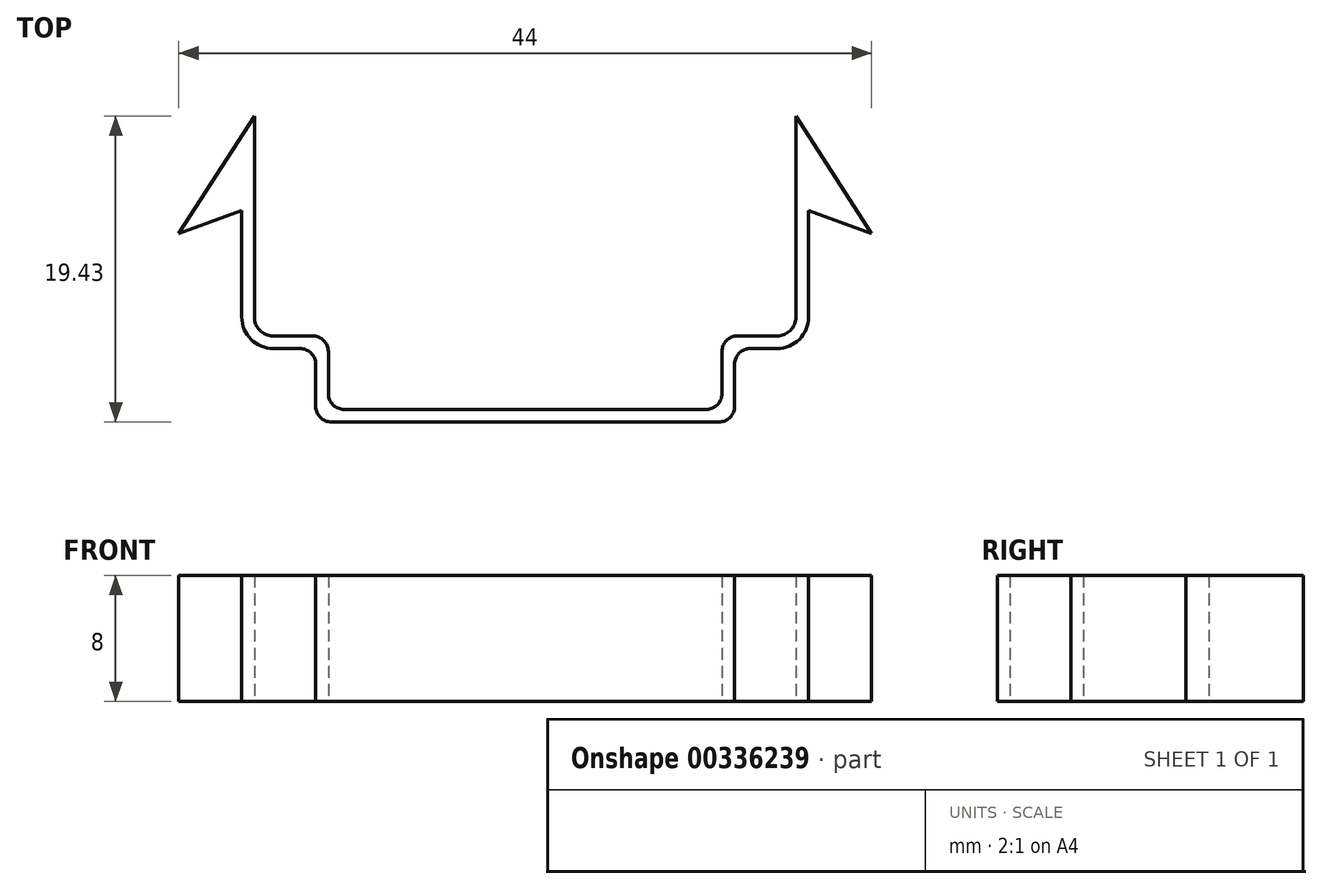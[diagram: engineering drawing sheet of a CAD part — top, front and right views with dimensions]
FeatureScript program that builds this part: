
annotation { "Feature Type Name" : "Feature", "Feature Type Description" : "" }
export const myFeature = defineFeature(function(context is Context, id is Id, definition is map)
    precondition{}
    {
        {
            var Q0;
            Q0=qCreatedBy(makeId("Top.planeOp"),FACE);
            var sketch = newSketch(context, id + "F0", { "sketchPlane" : qUnion([Q0])});
            skLineSegment(sketch, "E0.bottom", {"start": v(-12.5, 0) * mm, "end": v(12.5, 0) * mm});
            skLineSegment(sketch, "E0.top", {"start": v(-12.5, -7.73) * mm, "end": v(12.5, -7.73) * mm});
            skLineSegment(sketch, "E0.left", {"start": v(-12.5, 0) * mm, "end": v(-12.5, -7.73) * mm});
            skLineSegment(sketch, "E0.right", {"start": v(12.5, 0) * mm, "end": v(12.5, -7.73) * mm});
            skLineSegment(sketch, "E1.bottom", {"start": v(-18, 0) * mm, "end": v(-26.07, 0) * mm});
            skLineSegment(sketch, "E1.top", {"start": v(-18, 4.9) * mm, "end": v(-26.07, 4.9) * mm});
            skLineSegment(sketch, "E1.left", {"start": v(-18, 0) * mm, "end": v(-18, 4.9) * mm});
            skLineSegment(sketch, "E1.right", {"start": v(-26.07, 0) * mm, "end": v(-26.07, 4.9) * mm});
            skLineSegment(sketch, "E2.MirrorCS", {"start": v(18, 0) * mm, "end": v(18, 4.9) * mm});
            skLineSegment(sketch, "E3.MirrorCS", {"start": v(18, 4.9) * mm, "end": v(26.07, 4.9) * mm});
            skLineSegment(sketch, "E4.MirrorCS", {"start": v(26.07, 0) * mm, "end": v(26.07, 4.9) * mm});
            skLineSegment(sketch, "E5.MirrorCS", {"start": v(18, 0) * mm, "end": v(26.07, 0) * mm});
            skSolve(sketch);
        }
        {
            var Q0;
            Q0=qCreatedBy(makeId("Top.planeOp"),FACE);
            var sketch = newSketch(context, id + "F1", { "sketchPlane" : qUnion([Q0])});
            skLineSegment(sketch, "E6.0.0", {"start": v(-12.5, 0) * mm, "end": v(-12.5, -7.73) * mm, "construction": true});
            skLineSegment(sketch, "E6.0.1", {"start": v(-12.5, -7.73) * mm, "end": v(12.5, -7.73) * mm, "construction": true});
            skLineSegment(sketch, "E6.0.2", {"start": v(12.5, -7.73) * mm, "end": v(12.5, 0) * mm, "construction": true});
            skLineSegment(sketch, "E6.0.3", {"start": v(12.5, 0) * mm, "end": v(-12.5, 0) * mm, "construction": true});
            skLineSegment(sketch, "E7.0.0", {"start": v(-18, 0) * mm, "end": v(-18, 4.9) * mm, "construction": true});
            skLineSegment(sketch, "E7.0.1", {"start": v(-18, 4.9) * mm, "end": v(-26.07, 4.9) * mm, "construction": true});
            skLineSegment(sketch, "E7.0.2", {"start": v(-26.07, 4.9) * mm, "end": v(-26.07, 0) * mm, "construction": true});
            skLineSegment(sketch, "E7.0.3", {"start": v(-26.07, 0) * mm, "end": v(-18, 0) * mm, "construction": true});
            skLineSegment(sketch, "E8.0.0", {"start": v(18, 4.9) * mm, "end": v(18, 0) * mm, "construction": true});
            skLineSegment(sketch, "E8.0.1", {"start": v(18, 0) * mm, "end": v(26.07, 0) * mm, "construction": true});
            skLineSegment(sketch, "E8.0.2", {"start": v(26.07, 0) * mm, "end": v(26.07, 4.9) * mm, "construction": true});
            skLineSegment(sketch, "E8.0.3", {"start": v(26.07, 4.9) * mm, "end": v(18, 4.9) * mm, "construction": true});
            skLineSegment(sketch, "E9", {"start": v(-12.5, -3.87) * mm, "end": v(-16, -3.87) * mm});
            skLineSegment(sketch, "E10", {"start": v(-18, -1.87) * mm, "end": v(-18, 4.9) * mm});
            skLineSegment(sketch, "E11", {"start": v(-18, 4.9) * mm, "end": v(-22, 3.44) * mm});
            skLineSegment(sketch, "E12", {"start": v(-22, 3.44) * mm, "end": v(-17.2, 10.9) * mm});
            skPoint(sketch, "E13.visualSharp", {"position": v(-18, -3.87) * mm});
            skArc(sketch, "E13.filletArc", {"start": v(-18, -1.87) * mm, "mid": v(-17.41, -3.28) * mm, "end": v(-16, -3.87) * mm});
            skLineSegment(sketch, "E14.0", {"start": v(-17.2, -1.87) * mm, "end": v(-17.2, 10.9) * mm});
            skArc(sketch, "E14.1", {"start": v(-17.2, -1.87) * mm, "mid": v(-16.85, -2.71) * mm, "end": v(-16, -3.07) * mm});
            skLineSegment(sketch, "E14.2", {"start": v(-12.5, -3.07) * mm, "end": v(-16, -3.07) * mm});
            skLineSegment(sketch, "E15", {"start": v(-12.5, -3.07) * mm, "end": v(-12.5, -3.87) * mm});
            skLineSegment(sketch, "E16", {"start": v(-12.5, -3.87) * mm, "end": v(-12.5, -7.73) * mm});
            skLineSegment(sketch, "E17", {"start": v(-12.5, -7.73) * mm, "end": v(0, -7.73) * mm});
            skLineSegment(sketch, "E18.0", {"start": v(-13.3, -8.53) * mm, "end": v(0, -8.53) * mm});
            skLineSegment(sketch, "E18.1", {"start": v(-13.3, -3.87) * mm, "end": v(-13.3, -8.53) * mm});
            skLineSegment(sketch, "E19.MirrorCS", {"start": v(17.2, -1.87) * mm, "end": v(17.2, 10.9) * mm});
            skLineSegment(sketch, "E20.MirrorCS", {"start": v(22, 3.44) * mm, "end": v(17.2, 10.9) * mm});
            skLineSegment(sketch, "E21.MirrorCS", {"start": v(18, 4.9) * mm, "end": v(22, 3.44) * mm});
            skLineSegment(sketch, "E22.MirrorCS", {"start": v(18, 0) * mm, "end": v(18, 4.9) * mm, "construction": true});
            skArc(sketch, "E23.MirrorCS", {"start": v(18, -1.87) * mm, "mid": v(17.41, -3.28) * mm, "end": v(16, -3.87) * mm});
            skArc(sketch, "E24.MirrorCS", {"start": v(17.2, -1.87) * mm, "mid": v(16.85, -2.71) * mm, "end": v(16, -3.07) * mm});
            skLineSegment(sketch, "E25.MirrorCS", {"start": v(12.5, -3.87) * mm, "end": v(16, -3.87) * mm});
            skLineSegment(sketch, "E26.MirrorCS", {"start": v(12.5, -3.07) * mm, "end": v(16, -3.07) * mm});
            skLineSegment(sketch, "E27.MirrorCS", {"start": v(13.3, -8.53) * mm, "end": v(0, -8.53) * mm});
            skLineSegment(sketch, "E28.MirrorCS", {"start": v(12.5, -7.73) * mm, "end": v(0, -7.73) * mm});
            skLineSegment(sketch, "E29.MirrorCS", {"start": v(13.3, -3.87) * mm, "end": v(13.3, -8.53) * mm});
            skLineSegment(sketch, "E30.MirrorCS", {"start": v(12.5, -3.87) * mm, "end": v(12.5, -7.73) * mm});
            skLineSegment(sketch, "E31.MirrorCS", {"start": v(12.5, -3.07) * mm, "end": v(12.5, -3.87) * mm});
            skLineSegment(sketch, "E32.MirrorCS", {"start": v(18, -1.87) * mm, "end": v(18, 4.9) * mm});
            skSolve(sketch);
        }
        {
            var Q0;
            Q0 = qSketchRegion(id + "F1", true);
            extrude(context, id + "F2", {"entities" : qUnion([Q0]), "depth" : 8 * mm, "offsetDistance" : 25 * mm});
        }
        {
            var Q0;
            Q0=makeQuery(id+"F2.opExtrude","SWEPT_EDGE",EDGE,{"disambiguationData":[OSD([sQuery(id+"F1.wireOp",EDGE,"E9"),sQuery(id+"F1.wireOp",EDGE,"E18.1")])]});
            var Q1;
            Q1=makeQuery(id+"F2.opExtrude","SWEPT_EDGE",EDGE,{"disambiguationData":[OSD([sQuery(id+"F1.wireOp",EDGE,"E25.MirrorCS"),sQuery(id+"F1.wireOp",EDGE,"E29.MirrorCS")])]});
            var Q2;
            Q2=makeQuery(id+"F2.opExtrude","SWEPT_EDGE",EDGE,{"disambiguationData":[OSD([sQuery(id+"F1.wireOp",EDGE,"E14.2"),sQuery(id+"F1.wireOp",EDGE,"E15")])]});
            var Q3;
            Q3=makeQuery(id+"F2.opExtrude","SWEPT_EDGE",EDGE,{"disambiguationData":[OSD([sQuery(id+"F1.wireOp",EDGE,"E26.MirrorCS"),sQuery(id+"F1.wireOp",EDGE,"E31.MirrorCS")])]});
            var Q4;
            Q4=makeQuery(id+"F2.opExtrude","SWEPT_EDGE",EDGE,{"disambiguationData":[OSD([sQuery(id+"F1.wireOp",EDGE,"E18.0"),sQuery(id+"F1.wireOp",EDGE,"E18.1")])]});
            var Q5;
            Q5=makeQuery(id+"F2.opExtrude","SWEPT_EDGE",EDGE,{"disambiguationData":[OSD([sQuery(id+"F1.wireOp",EDGE,"E16"),sQuery(id+"F1.wireOp",EDGE,"E17")])]});
            var Q6;
            Q6=makeQuery(id+"F2.opExtrude","SWEPT_EDGE",EDGE,{"disambiguationData":[OSD([sQuery(id+"F1.wireOp",EDGE,"E27.MirrorCS"),sQuery(id+"F1.wireOp",EDGE,"E29.MirrorCS")])]});
            var Q7;
            Q7=makeQuery(id+"F2.opExtrude","SWEPT_EDGE",EDGE,{"disambiguationData":[OSD([sQuery(id+"F1.wireOp",EDGE,"E28.MirrorCS"),sQuery(id+"F1.wireOp",EDGE,"E30.MirrorCS")])]});
            fillet(context, id + "F3", {"entities" : qUnion([Q0, Q1, Q2, Q3, Q4, Q5, Q6, Q7]), "radius" : 1 * mm, "allowEdgeOverflow" : false});
        }
    });
